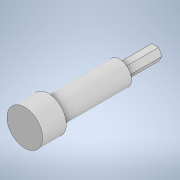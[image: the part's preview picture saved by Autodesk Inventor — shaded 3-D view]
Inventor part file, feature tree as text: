
AUTODESK INVENTOR PART (.ipt)
format: ipt  version: 2022.2 (Build 262287010, 287A)  size: 116,224 bytes
history: native  units: in
note: dims shown in document units (in); Inventor stores cm internally (conversion verified against a paired STEP export)
features: extrude x3, sketch x3
ambient origin geometry x8: Origin, YZ Plane, XZ Plane, XY Plane, X Axis, Y Axis, Z Axis, Center Point
bodies: Solid1 (feature_tree)
feature tree (6):
  extrude  "Extrusion1"  Depth=1.0in TaperAngle=0.0deg
  extrude  "Extrusion2"  Depth=3.0in TaperAngle=0.0deg
  extrude  "Extrusion3"  Depth=1.5in TaperAngle=0.0deg
  sketch  "Sketch1"  dims[d0=1.5in d1=1.0in d2=0.0in]
  sketch  "Sketch3"  dims[d4=1.0in d5=3.0in d6=0.0in]
  sketch  "Sketch4"  dims[d7=0.5in d8=1.5in d9=0.0in]
